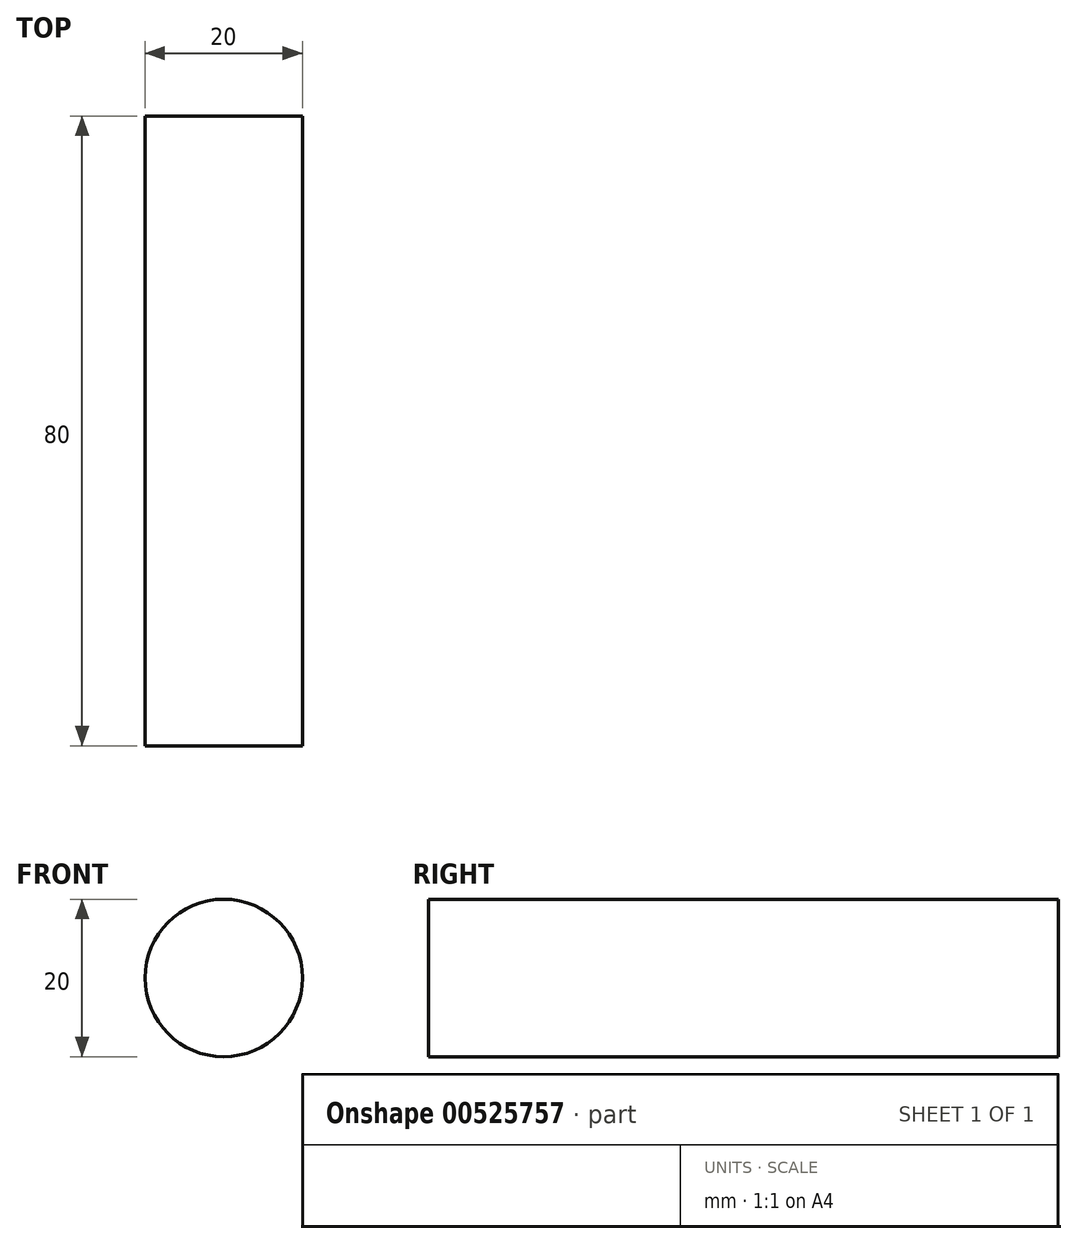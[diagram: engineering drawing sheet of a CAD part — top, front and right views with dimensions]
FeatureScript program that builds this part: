
annotation { "Feature Type Name" : "Feature", "Feature Type Description" : "" }
export const myFeature = defineFeature(function(context is Context, id is Id, definition is map)
    precondition{}
    {
        {
            var Q0;
            Q0=qCreatedBy(makeId("Front.planeOp"),FACE);
            var sketch = newSketch(context, id + "F0", { "sketchPlane" : qUnion([Q0])});
            skCircle(sketch, "E0", {"center": v(0, 0) * mm, "radius": 10 * mm});
            skSolve(sketch);
        }
        {
            var Q0;
            Q0 = qSketchRegion(id + "F0", true);
            extrude(context, id + "F1", {"entities" : qUnion([Q0]), "depth" : 80 * mm, "offsetDistance" : 25 * mm});
        }
    });
